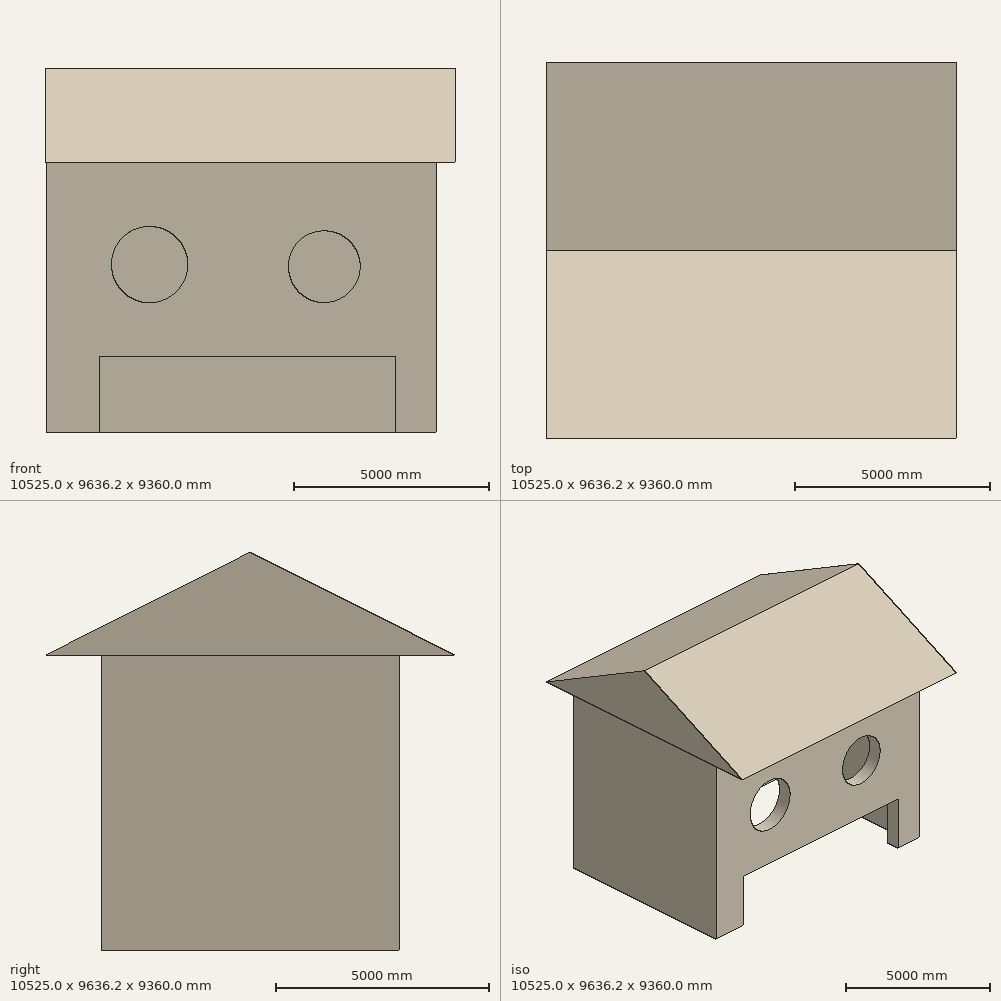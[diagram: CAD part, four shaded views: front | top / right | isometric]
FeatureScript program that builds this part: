
annotation { "Feature Type Name" : "Feature", "Feature Type Description" : "" }
export const myFeature = defineFeature(function(context is Context, id is Id, definition is map)
    precondition{}
    {
        {
            var Q0;
            Q0=qCreatedBy(makeId("Top.planeOp"),FACE);
            var sketch = newSketch(context, id + "F0", { "sketchPlane" : qUnion([Q0])});
            skLineSegment(sketch, "E0.bottom", {"start": v(-5000.34, 4472.78) * mm, "end": v(4999.66, 4472.78) * mm});
            skLineSegment(sketch, "E0.top", {"start": v(-5000.34, -2527.22) * mm, "end": v(4999.66, -2527.22) * mm});
            skLineSegment(sketch, "E0.left", {"start": v(-5000.34, 4472.78) * mm, "end": v(-5000.34, -2527.22) * mm});
            skLineSegment(sketch, "E0.right", {"start": v(4999.66, 4472.78) * mm, "end": v(4999.66, -2527.22) * mm});
            skLineSegment(sketch, "E1.bottom", {"start": v(-4558.33, 3860.06) * mm, "end": v(4574.24, 3860.06) * mm});
            skLineSegment(sketch, "E1.top", {"start": v(-4558.33, -2012.1) * mm, "end": v(4574.24, -2012.1) * mm});
            skLineSegment(sketch, "E1.left", {"start": v(-4558.33, 3860.06) * mm, "end": v(-4558.33, -2012.1) * mm});
            skLineSegment(sketch, "E1.right", {"start": v(4574.24, 3860.06) * mm, "end": v(4574.24, -2012.1) * mm});
            skLineSegment(sketch, "E2", {"start": v(-3636.54, 4472.78) * mm, "end": v(-3636.54, 3860.06) * mm});
            skLineSegment(sketch, "E3", {"start": v(-1911.89, 4472.78) * mm, "end": v(-1911.89, 3860.06) * mm});
            skLineSegment(sketch, "E4", {"start": v(4574.24, 2734.42) * mm, "end": v(4999.66, 2734.42) * mm});
            skLineSegment(sketch, "E5", {"start": v(4574.24, 1670.57) * mm, "end": v(4999.66, 1670.57) * mm});
            skLineSegment(sketch, "E6", {"start": v(3949.3, -2012.1) * mm, "end": v(3949.3, -2527.22) * mm});
            skLineSegment(sketch, "E7", {"start": v(-3638.12, -2012.1) * mm, "end": v(-3638.12, -2527.22) * mm});
            skLineSegment(sketch, "E8", {"start": v(-366.3, 4472.78) * mm, "end": v(-366.3, 3860.06) * mm});
            skLineSegment(sketch, "E9", {"start": v(3728.5, 4472.78) * mm, "end": v(3728.5, 3860.06) * mm});
            skLineSegment(sketch, "E10", {"start": v(-5000.34, 2272.75) * mm, "end": v(-4558.33, 2272.75) * mm});
            skLineSegment(sketch, "E11", {"start": v(-5000.34, -437.04) * mm, "end": v(-4558.33, -437.04) * mm});
            skLineSegment(sketch, "E12", {"start": v(4999.66, 2734.42) * mm, "end": v(4999.66, 1670.57) * mm});
            skLineSegment(sketch, "E13", {"start": v(-5000.34, 2272.75) * mm, "end": v(-5000.34, -437.04) * mm});
            skLineSegment(sketch, "E14", {"start": v(-3638.12, -2527.22) * mm, "end": v(3949.3, -2527.22) * mm});
            skLineSegment(sketch, "E15", {"start": v(-366.3, 4472.78) * mm, "end": v(3728.5, 4472.78) * mm});
            skSolve(sketch);
        }
        {
            var Q0;
            {var subQ7=sQuery(id+"F0.wireOp",EDGE,"E2");Q0=makeQuery(id+"F0.imprint","IMPRINT",FACE,{"disambiguationData":[TD([[makeQuery(id+"F0.imprint","IMPRINT",EDGE,{"derivedFrom":subQ7}),-1.0]])]});}
            var Q1;
            {var subQ0=sQuery(id+"F0.wireOp",EDGE,"E2");Q1=makeQuery(id+"F0.imprint","IMPRINT",FACE,{"disambiguationData":[TD([[makeQuery(id+"F0.imprint","IMPRINT",EDGE,{"derivedFrom":subQ0}),1.0]])]});}
            var Q2;
            {var subQ0=sQuery(id+"F0.wireOp",EDGE,"E3");Q2=makeQuery(id+"F0.imprint","IMPRINT",FACE,{"disambiguationData":[TD([[makeQuery(id+"F0.imprint","IMPRINT",EDGE,{"derivedFrom":subQ0}),1.0]])]});}
            var Q3;
            {var subQ3=sQuery(id+"F0.wireOp",EDGE,"E4");Q3=makeQuery(id+"F0.imprint","IMPRINT",FACE,{"disambiguationData":[TD([[makeQuery(id+"F0.imprint","IMPRINT",EDGE,{"derivedFrom":subQ3}),1.0]])]});}
            var Q4;
            {var subQ4=sQuery(id+"F0.wireOp",EDGE,"E7");Q4=makeQuery(id+"F0.imprint","IMPRINT",FACE,{"disambiguationData":[TD([[makeQuery(id+"F0.imprint","IMPRINT",EDGE,{"derivedFrom":subQ4}),-1.0]])]});}
            var Q5;
            {var subQ3=sQuery(id+"F0.wireOp",EDGE,"E5");Q5=makeQuery(id+"F0.imprint","IMPRINT",FACE,{"disambiguationData":[TD([[makeQuery(id+"F0.imprint","IMPRINT",EDGE,{"derivedFrom":subQ3}),-1.0]])]});}
            var Q6;
            {var subQ0=sQuery(id+"F0.wireOp",EDGE,"E8");Q6=makeQuery(id+"F0.imprint","IMPRINT",FACE,{"disambiguationData":[TD([[makeQuery(id+"F0.imprint","IMPRINT",EDGE,{"derivedFrom":subQ0}),1.0]])]});}
            var Q7;
            {var subQ0=sQuery(id+"F0.wireOp",EDGE,"E6");Q7=makeQuery(id+"F0.imprint","IMPRINT",FACE,{"disambiguationData":[TD([[makeQuery(id+"F0.imprint","IMPRINT",EDGE,{"derivedFrom":subQ0}),-1.0]])]});}
            var Q8;
            {var subQ0=sQuery(id+"F0.wireOp",EDGE,"E10");Q8=makeQuery(id+"F0.imprint","IMPRINT",FACE,{"disambiguationData":[TD([[makeQuery(id+"F0.imprint","IMPRINT",EDGE,{"derivedFrom":subQ0}),-1.0]])]});}
            var Q9;
            {var subQ0=sQuery(id+"F0.wireOp",EDGE,"E4");Q9=makeQuery(id+"F0.imprint","IMPRINT",FACE,{"disambiguationData":[TD([[makeQuery(id+"F0.imprint","IMPRINT",EDGE,{"derivedFrom":subQ0}),-1.0]])]});}
            var Q10;
            Q10 = qSketchRegion(id + "F2", true);
            extrude(context, id + "F1", {"entities" : qUnion([Q0, Q1, Q2, Q3, Q4, Q5, Q6, Q7, Q8, Q9, Q10]), "depth" : 6940 * mm, "offsetDistance" : 25 * mm});
        }
        {
            var Q0;
            Q0=makeQuery(id+"F1.opExtrude","SWEPT_FACE",FACE,{"disambiguationData":[OSD([sQuery(id+"F0.wireOp",EDGE,"E0.top"),sQuery(id+"F0.wireOp",EDGE,"E14")])]});
            var sketch = newSketch(context, id + "F2", { "sketchPlane" : qUnion([Q0])});
            skLineSegment(sketch, "E16.bottom", {"start": v(-3638.12, 0) * mm, "end": v(3949.3, 0) * mm});
            skLineSegment(sketch, "E16.top", {"start": v(-3638.12, 1964.67) * mm, "end": v(3949.3, 1964.67) * mm});
            skLineSegment(sketch, "E16.left", {"start": v(-3638.12, 0) * mm, "end": v(-3638.12, 1964.67) * mm});
            skLineSegment(sketch, "E16.right", {"start": v(3949.3, 0) * mm, "end": v(3949.3, 1964.67) * mm});
            skSolve(sketch);
        }
        {
            var Q0;
            Q0=makeQuery(id+"F2.imprint","IMPRINT",FACE,{"disambiguationData":[TD([[makeQuery(id+"F2.imprint","IMPRINT",EDGE,{"derivedFrom":sQuery(id+"F2.wireOp",EDGE,"E16.bottom")}),1.0]])]});
            extrude(context, id + "F3", {"entities" : qUnion([Q0]), "operationType" : NewBodyOperationType.REMOVE, "endBound" : BoundingType.UP_TO_NEXT, "oppositeDirection" : true, "depth" : 25 * mm, "offsetDistance" : 25 * mm});
        }
        {
            var Q0;
            Q0=makeQuery(id+"F1.opExtrude","SWEPT_FACE",FACE,{"disambiguationData":[OSD([sQuery(id+"F0.wireOp",EDGE,"E0.left"),sQuery(id+"F0.wireOp",EDGE,"E13")])]});
            var sketch = newSketch(context, id + "F4", { "sketchPlane" : qUnion([Q0])});
            skLineSegment(sketch, "E17", {"start": v(-5797.18, 6940) * mm, "end": v(-972.78, 9359.95) * mm});
            skPoint(sketch, "E17.endSnap0", {"position": v(-972.78, 6940) * mm});
            skLineSegment(sketch, "E18", {"start": v(-972.78, 9359.95) * mm, "end": v(3839, 6940) * mm});
            skLineSegment(sketch, "E19", {"start": v(3839, 6940) * mm, "end": v(-5797.18, 6940) * mm});
            skSolve(sketch);
        }
        {
            var Q0;
            {var subQ5=sQuery(id+"F4.wireOp",EDGE,"E17");Q0=makeQuery(id+"F4.imprint","IMPRINT",FACE,{"disambiguationData":[TD([[makeQuery(id+"F4.imprint","IMPRINT",EDGE,{"derivedFrom":subQ5}),-1.0]])]});}
            extrude(context, id + "F5", {"entities" : qUnion([Q0]), "operationType" : NewBodyOperationType.ADD, "depth" : 25 * mm, "offsetDistance" : 25 * mm, "hasSecondDirection" : true, "secondDirectionOppositeDirection" : true, "secondDirectionDepth" : 10500 * mm});
        }
        {
            var Q0;
            Q0=makeQuery(id+"F1.opExtrude","SWEPT_FACE",FACE,{"disambiguationData":[OSD([sQuery(id+"F0.wireOp",EDGE,"E0.top"),sQuery(id+"F0.wireOp",EDGE,"E14")])]});
            var sketch = newSketch(context, id + "F6", { "sketchPlane" : qUnion([Q0])});
            skCircle(sketch, "E20", {"center": v(-2351, 4316.58) * mm, "radius": 979.46 * mm});
            skCircle(sketch, "E21", {"center": v(2133.88, 4263.7) * mm, "radius": 921.95 * mm});
            skSolve(sketch);
        }
        {
            var Q0;
            Q0=makeQuery(id+"F6.imprint","IMPRINT",FACE,{"disambiguationData":[TD([[makeQuery(id+"F6.imprint","IMPRINT",EDGE,{"derivedFrom":sQuery(id+"F6.wireOp",EDGE,"E20")}),1.0]])]});
            extrude(context, id + "F7", {"entities" : qUnion([Q0]), "operationType" : NewBodyOperationType.REMOVE, "endBound" : BoundingType.UP_TO_NEXT, "oppositeDirection" : true, "depth" : 25 * mm, "offsetDistance" : 25 * mm});
        }
        {
            var Q0;
            Q0=makeQuery(id+"F6.imprint","IMPRINT",FACE,{"disambiguationData":[TD([[makeQuery(id+"F6.imprint","IMPRINT",EDGE,{"derivedFrom":sQuery(id+"F6.wireOp",EDGE,"E20")}),1.0]])]});
            var Q1;
            Q1=makeQuery(id+"F6.imprint","IMPRINT",FACE,{"disambiguationData":[TD([[makeQuery(id+"F6.imprint","IMPRINT",EDGE,{"derivedFrom":sQuery(id+"F6.wireOp",EDGE,"E21")}),1.0]])]});
            extrude(context, id + "F8", {"entities" : qUnion([Q0, Q1]), "operationType" : NewBodyOperationType.REMOVE, "endBound" : BoundingType.UP_TO_NEXT, "oppositeDirection" : true, "depth" : 25 * mm, "offsetDistance" : 25 * mm});
        }
    });
